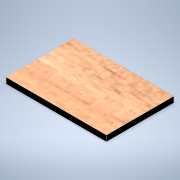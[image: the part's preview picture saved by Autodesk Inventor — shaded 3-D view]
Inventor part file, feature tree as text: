
AUTODESK INVENTOR PART (.ipt)
format: ipt  version: 2021 (Build 250183000, 183)  size: 119,296 bytes
history: native  units: mm
features: extrude x2, sketch x2
ambient origin geometry x8: Origin, YZ Plane, XZ Plane, XY Plane, X Axis, Y Axis, Z Axis, Center Point
bodies: Volumenkörper1 (feature_tree)
feature tree (4):
  extrude  "Extrusion1"  Depth=52.0mm
  extrude  "Extrusion2"  Depth=52.0mm
  sketch  "Skizze1"  dims[d0=35.0mm d1=52.0mm]
  sketch  "Skizze2"  dims[d2=3.0mm d3=0.0mm d4=52.0mm d5=35.0mm d6=3.0mm d7=0.0mm]
